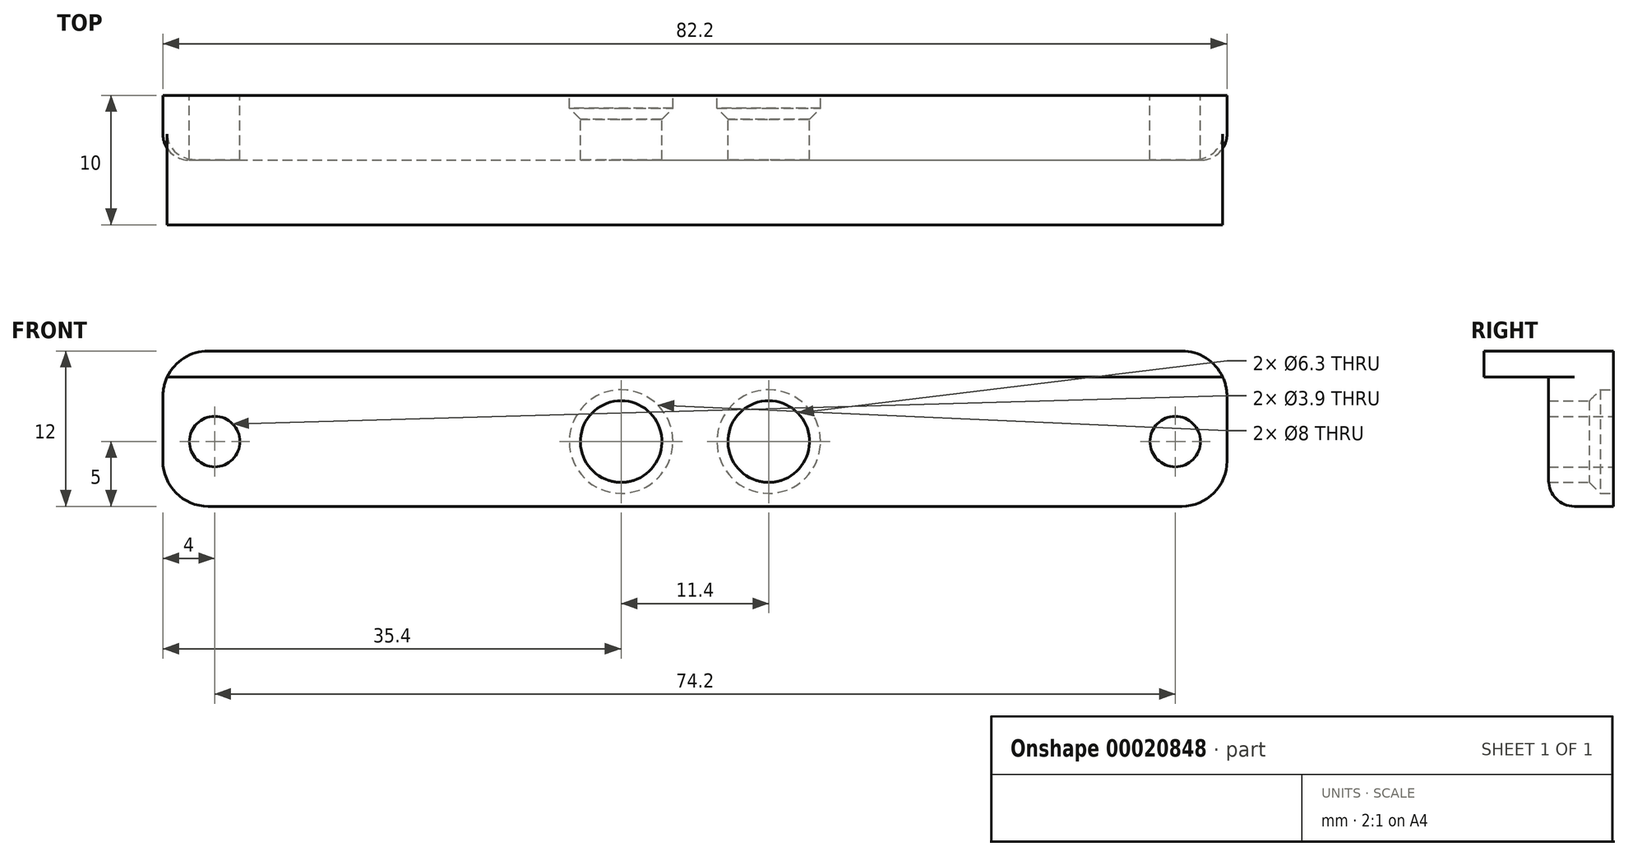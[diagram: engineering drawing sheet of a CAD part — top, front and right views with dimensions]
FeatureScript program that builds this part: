
annotation { "Feature Type Name" : "Feature", "Feature Type Description" : "" }
export const myFeature = defineFeature(function(context is Context, id is Id, definition is map)
    precondition{}
    {
        {
            var Q0;
            Q0=qCreatedBy(makeId("Front.planeOp"),FACE);
            var sketch = newSketch(context, id + "F0", { "sketchPlane" : qUnion([Q0])});
            skLineSegment(sketch, "E0.rect.bottom", {"start": v(-41.1, 5) * mm, "end": v(41.1, 5) * mm});
            skLineSegment(sketch, "E0.rect.top", {"start": v(-41.1, -5) * mm, "end": v(41.1, -5) * mm});
            skLineSegment(sketch, "E0.rect.left", {"start": v(-41.1, 5) * mm, "end": v(-41.1, -5) * mm});
            skLineSegment(sketch, "E0.rect.right", {"start": v(41.1, 5) * mm, "end": v(41.1, -5) * mm});
            skPoint(sketch, "E0.rect.middle", {"position": v(0, 0) * mm});
            skCircle(sketch, "E1", {"center": v(-37.1, 0) * mm, "radius": 1.95 * mm});
            skCircle(sketch, "E2.MirrorC", {"center": v(37.1, 0) * mm, "radius": 1.95 * mm});
            skSolve(sketch);
        }
        {
            var Q0;
            Q0 = qSketchRegion(id + "F0", true);
            extrude(context, id + "F1", {"entities" : qUnion([Q0]), "depth" : 5 * mm});
        }
        {
            var Q0;
            Q0=makeQuery(id+"F1.opExtrude","CAP_FACE",FACE,{"disambiguationData":[OSD([sQuery(id+"F0.wireOp",EDGE,"E0.rect.bottom"),sQuery(id+"F0.wireOp",EDGE,"E0.rect.top"),sQuery(id+"F0.wireOp",EDGE,"E0.rect.left"),sQuery(id+"F0.wireOp",EDGE,"E0.rect.right"),sQuery(id+"F0.wireOp",EDGE,"E1"),sQuery(id+"F0.wireOp",EDGE,"E2.MirrorC")])],"isStart":true});
            var sketch = newSketch(context, id + "F2", { "sketchPlane" : qUnion([Q0])});
            skCircle(sketch, "E3", {"center": v(5.7, 0) * mm, "radius": 3.15 * mm});
            skCircle(sketch, "E4.MirrorC", {"center": v(-5.7, 0) * mm, "radius": 3.15 * mm});
            skSolve(sketch);
        }
        {
            var Q0;
            Q0 = qSketchRegion(id + "F2", true);
            extrude(context, id + "F3", {"entities" : qUnion([Q0]), "operationType" : NewBodyOperationType.REMOVE, "endBound" : BoundingType.THROUGH_ALL, "oppositeDirection" : true, "depth" : 4 * mm});
        }
        {
            var Q0;
            Q0=makeQuery(id+"F1.opExtrude","CAP_FACE",FACE,{"disambiguationData":[OSD([sQuery(id+"F0.wireOp",EDGE,"E0.rect.bottom"),sQuery(id+"F0.wireOp",EDGE,"E0.rect.top"),sQuery(id+"F0.wireOp",EDGE,"E0.rect.left"),sQuery(id+"F0.wireOp",EDGE,"E0.rect.right"),sQuery(id+"F0.wireOp",EDGE,"E1"),sQuery(id+"F0.wireOp",EDGE,"E2.MirrorC")])],"isStart":true});
            var sketch = newSketch(context, id + "F4", { "sketchPlane" : qUnion([Q0])});
            skCircle(sketch, "E5", {"center": v(5.7, 0) * mm, "radius": 4 * mm});
            skCircle(sketch, "E6.MirrorC", {"center": v(-5.7, 0) * mm, "radius": 4 * mm});
            skSolve(sketch);
        }
        {
            var Q0;
            Q0 = qSketchRegion(id + "F4", true);
            extrude(context, id + "F5", {"entities" : qUnion([Q0]), "operationType" : NewBodyOperationType.REMOVE, "oppositeDirection" : true, "depth" : 2 * mm});
        }
        {
            var Q0;
            Q0=makeQuery(id+"F5.boolean.opBoolean","COPY",EDGE,{"derivedFrom":makeQuery(id+"F5.opExtrude","CAP_EDGE",EDGE,{"disambiguationData":[OSD([sQuery(id+"F4.wireOp",EDGE,"E6.MirrorC")])],"isStart":false})});
            var Q1;
            Q1=makeQuery(id+"F5.boolean.opBoolean","COPY",EDGE,{"derivedFrom":makeQuery(id+"F5.opExtrude","CAP_EDGE",EDGE,{"disambiguationData":[OSD([sQuery(id+"F4.wireOp",EDGE,"E5")])],"isStart":false})});
            chamfer(context, id + "F6", {"entities" : qUnion([Q0, Q1]), "width" : 1 * mm, "tangentPropagation" : true});
        }
        {
            var Q0;
            Q0=makeQuery(id+"F1.opExtrude","SWEPT_FACE",FACE,{"disambiguationData":[OSD([sQuery(id+"F0.wireOp",EDGE,"E0.rect.bottom")])]});
            var sketch = newSketch(context, id + "F7", { "sketchPlane" : qUnion([Q0])});
            skLineSegment(sketch, "E7.bottom", {"start": v(41.1, 0) * mm, "end": v(-41.1, 0) * mm});
            skLineSegment(sketch, "E7.top", {"start": v(41.1, -10) * mm, "end": v(-41.1, -10) * mm});
            skLineSegment(sketch, "E7.left", {"start": v(41.1, 0) * mm, "end": v(41.1, -10) * mm});
            skLineSegment(sketch, "E7.right", {"start": v(-41.1, 0) * mm, "end": v(-41.1, -10) * mm});
            skSolve(sketch);
        }
        {
            var Q0;
            Q0 = qSketchRegion(id + "F7", true);
            extrude(context, id + "F8", {"entities" : qUnion([Q0]), "operationType" : NewBodyOperationType.ADD, "depth" : 2 * mm});
        }
        {
            var Q0;
            Q0=makeQuery(id+"F1.opExtrude","SWEPT_EDGE",EDGE,{"disambiguationData":[OSD([sQuery(id+"F0.wireOp",EDGE,"E0.rect.top"),sQuery(id+"F0.wireOp",EDGE,"E0.rect.right")])]});
            var Q1;
            Q1=makeQuery(id+"F1.opExtrude","SWEPT_EDGE",EDGE,{"disambiguationData":[OSD([sQuery(id+"F0.wireOp",EDGE,"E0.rect.top"),sQuery(id+"F0.wireOp",EDGE,"E0.rect.left")])]});
            var Q2;
            Q2=makeQuery(id+"F8.opExtrude","CAP_EDGE",EDGE,{"disambiguationData":[OSD([sQuery(id+"F7.wireOp",EDGE,"E7.left")])],"isStart":false});
            var Q3;
            Q3=makeQuery(id+"F8.opExtrude","CAP_EDGE",EDGE,{"disambiguationData":[OSD([sQuery(id+"F7.wireOp",EDGE,"E7.right")])],"isStart":false});
            fillet(context, id + "F9", {"entities" : qUnion([Q0, Q1, Q2, Q3]), "radius" : 3.5 * mm, "tangentPropagation" : true, "allowEdgeOverflow" : false});
        }
        {
            var Q0;
            Q0=makeQuery(id+"F1.opExtrude","CAP_EDGE",EDGE,{"disambiguationData":[OSD([sQuery(id+"F0.wireOp",EDGE,"E0.rect.top")])],"isStart":false});
            fillet(context, id + "F10", {"entities" : qUnion([Q0]), "radius" : 2 * mm, "tangentPropagation" : true, "allowEdgeOverflow" : false});
        }
    });
